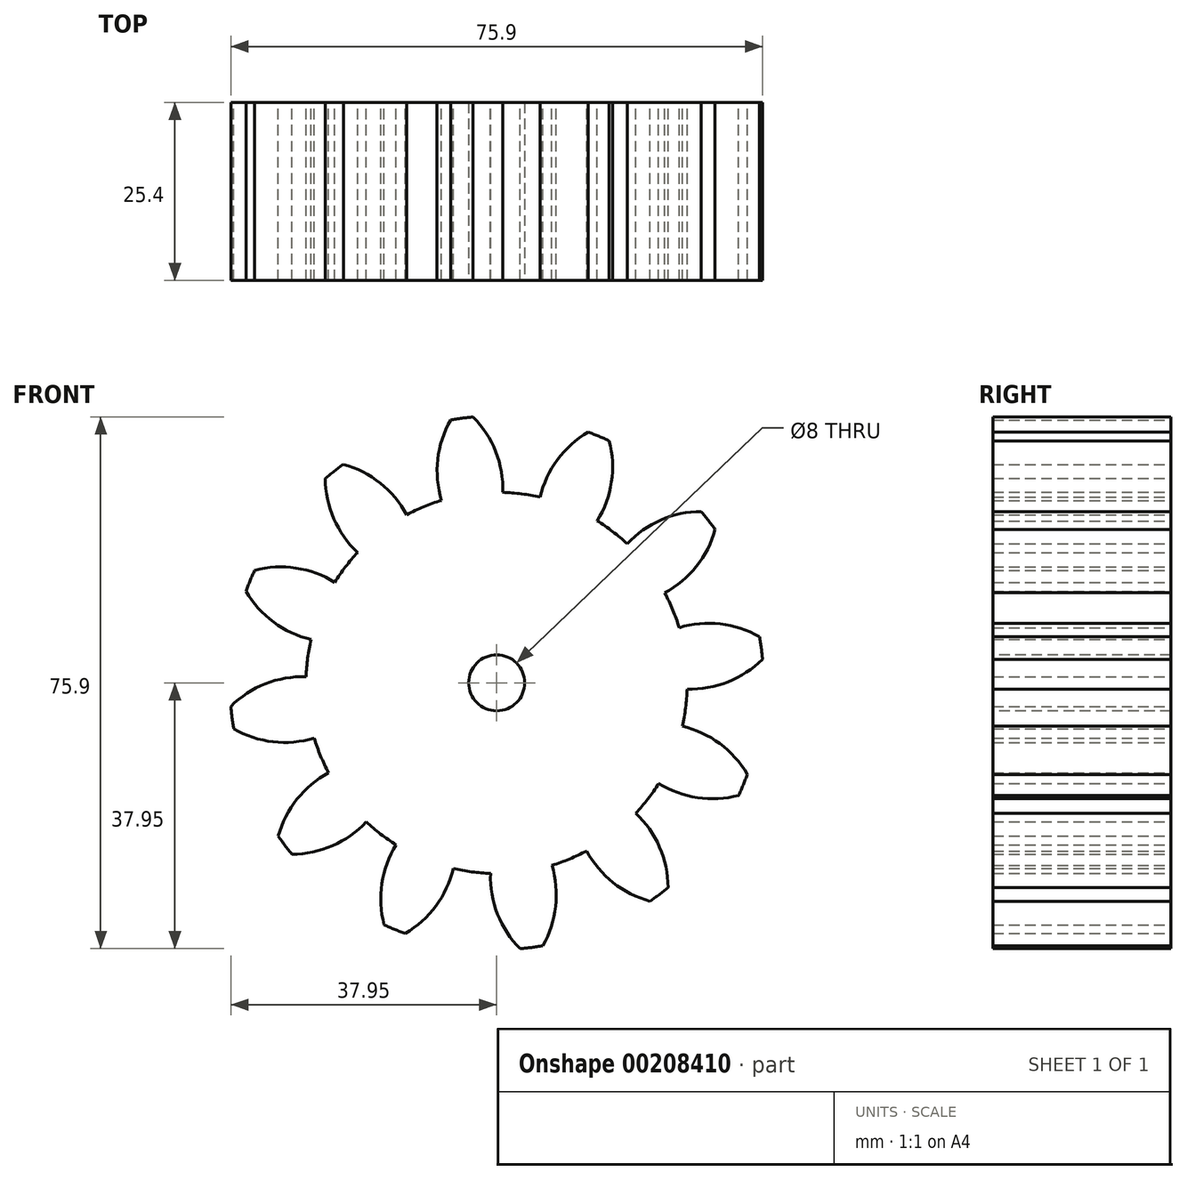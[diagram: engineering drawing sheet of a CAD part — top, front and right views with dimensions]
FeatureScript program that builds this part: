
annotation { "Feature Type Name" : "Feature", "Feature Type Description" : "" }
export const myFeature = defineFeature(function(context is Context, id is Id, definition is map)
    precondition{}
    {
        {
            assignVariable(context, id + "F0", {"name" : "NOT", "anyValue" : 12});
        }
        {
            var Q0;
            Q0=qCreatedBy(makeId("Front.planeOp"),FACE);
            var sketch = newSketch(context, id + "F1", { "sketchPlane" : qUnion([Q0])});
            skCircle(sketch, "E0", {"center": v(0, 0) * mm, "radius": 38.1 * mm});
            skCircle(sketch, "E1", {"center": v(0, 0) * mm, "radius": 32.66 * mm});
            skCircle(sketch, "E2", {"center": v(0, 0) * mm, "radius": 27.21 * mm});
            skLineSegment(sketch, "E3", {"start": v(0, 0) * mm, "end": v(0, 56.5) * mm});
            skLineSegment(sketch, "E4", {"start": v(0, 0) * mm, "end": v(-7.42, 56.35) * mm});
            skLineSegment(sketch, "E5", {"start": v(0, 32.66) * mm, "end": v(-56.68, 32.66) * mm});
            skLineSegment(sketch, "E6", {"start": v(0, 32.66) * mm, "end": v(-52.94, 13.39) * mm});
            skCircle(sketch, "E7", {"center": v(0, 32.66) * mm, "radius": 14.6 * mm});
            skArc(sketch, "E8", {"start": v(0.87, 27.2) * mm, "mid": v(-0.13, 33.01) * mm, "end": v(-3.36, 37.95) * mm});
            skArc(sketch, "E9.MirrorCS", {"start": v(-7.88, 26.05) * mm, "mid": v(-8.41, 31.92) * mm, "end": v(-6.58, 37.53) * mm});
            skSolve(sketch);
        }
        {
            var Q0;
            {var subQ0=sQuery(id+"F1.wireOp",EDGE,"E3");var subQ1=sQuery(id+"F1.wireOp",EDGE,"E2");var subQ2=makeQuery(id+"F1.imprint","INTERSECT",VERTEX,{"derivedFrom":[subQ1,subQ0]});Q0=makeQuery(id+"F1.imprint","IMPRINT",FACE,{"disambiguationData":[TD([[makeQuery(id+"F1.imprint","IMPRINT",EDGE,{"disambiguationData":[TD([[subQ2,-1.0]])],"derivedFrom":subQ1}),-1.0]])]});}
            var Q1;
            {var subQ0=sQuery(id+"F1.wireOp",EDGE,"E9.MirrorCS");var subQ1=sQuery(id+"F1.wireOp",EDGE,"E2");var subQ2=makeQuery(id+"F1.imprint","INTERSECT",VERTEX,{"derivedFrom":[subQ1,subQ0]});Q1=makeQuery(id+"F1.imprint","IMPRINT",FACE,{"disambiguationData":[TD([[makeQuery(id+"F1.imprint","IMPRINT",EDGE,{"disambiguationData":[TD([[subQ2,1.0]])],"derivedFrom":subQ1}),-1.0]])]});}
            var Q2;
            {var subQ0=sQuery(id+"F1.wireOp",EDGE,"E4");var subQ1=sQuery(id+"F1.wireOp",EDGE,"E1");var subQ2=makeQuery(id+"F1.imprint","INTERSECT",VERTEX,{"derivedFrom":[subQ1,subQ0]});Q2=makeQuery(id+"F1.imprint","IMPRINT",FACE,{"disambiguationData":[TD([[makeQuery(id+"F1.imprint","IMPRINT",EDGE,{"disambiguationData":[TD([[subQ2,-1.0]])],"derivedFrom":subQ1}),1.0]])]});}
            var Q3;
            {var subQ0=sQuery(id+"F1.wireOp",EDGE,"E4");var subQ1=sQuery(id+"F1.wireOp",EDGE,"E1");var subQ2=makeQuery(id+"F1.imprint","INTERSECT",VERTEX,{"derivedFrom":[subQ1,subQ0]});Q3=makeQuery(id+"F1.imprint","IMPRINT",FACE,{"disambiguationData":[TD([[makeQuery(id+"F1.imprint","IMPRINT",EDGE,{"disambiguationData":[TD([[subQ2,-1.0]])],"derivedFrom":subQ1}),-1.0]])]});}
            var Q4;
            {var subQ1=sQuery(id+"F1.wireOp",EDGE,"E1");var subQ3=sQuery(id+"F1.wireOp",EDGE,"E4");var subQ4=makeQuery(id+"F1.imprint","INTERSECT",VERTEX,{"derivedFrom":[subQ1,subQ3]});Q4=makeQuery(id+"F1.imprint","IMPRINT",FACE,{"disambiguationData":[TD([[makeQuery(id+"F1.imprint","IMPRINT",EDGE,{"disambiguationData":[TD([[subQ4,1.0]])],"derivedFrom":subQ3}),-1.0]])]});}
            var Q5;
            {var subQ1=sQuery(id+"F1.wireOp",EDGE,"E1");var subQ3=sQuery(id+"F1.wireOp",EDGE,"E4");var subQ4=makeQuery(id+"F1.imprint","INTERSECT",VERTEX,{"derivedFrom":[subQ1,subQ3]});Q5=makeQuery(id+"F1.imprint","IMPRINT",FACE,{"disambiguationData":[TD([[makeQuery(id+"F1.imprint","IMPRINT",EDGE,{"disambiguationData":[TD([[subQ4,-1.0]])],"derivedFrom":subQ3}),-1.0]])]});}
            var Q6;
            {var subQ0=sQuery(id+"F1.wireOp",EDGE,"E8");var subQ1=sQuery(id+"F1.wireOp",EDGE,"E0");var subQ2=makeQuery(id+"F1.imprint","INTERSECT",VERTEX,{"derivedFrom":[subQ1,subQ0]});Q6=makeQuery(id+"F1.imprint","IMPRINT",FACE,{"disambiguationData":[TD([[makeQuery(id+"F1.imprint","IMPRINT",EDGE,{"disambiguationData":[TD([[subQ2,-1.0]])],"derivedFrom":subQ1}),1.0]])]});}
            var Q7;
            {var subQ0=sQuery(id+"F1.wireOp",EDGE,"E9.MirrorCS");var subQ1=sQuery(id+"F1.wireOp",EDGE,"E0");var subQ2=makeQuery(id+"F1.imprint","INTERSECT",VERTEX,{"derivedFrom":[subQ1,subQ0]});Q7=makeQuery(id+"F1.imprint","IMPRINT",FACE,{"disambiguationData":[TD([[makeQuery(id+"F1.imprint","IMPRINT",EDGE,{"disambiguationData":[TD([[subQ2,1.0]])],"derivedFrom":subQ1}),1.0]])]});}
            var Q8;
            {var subQ0=sQuery(id+"F1.wireOp",EDGE,"E8");var subQ1=sQuery(id+"F1.wireOp",EDGE,"E2");var subQ2=makeQuery(id+"F1.imprint","INTERSECT",VERTEX,{"derivedFrom":[subQ1,subQ0]});Q8=makeQuery(id+"F1.imprint","IMPRINT",FACE,{"disambiguationData":[TD([[makeQuery(id+"F1.imprint","IMPRINT",EDGE,{"disambiguationData":[TD([[subQ2,-1.0]])],"derivedFrom":subQ1}),-1.0]])]});}
            var Q9;
            {var subQ0=sQuery(id+"F1.wireOp",EDGE,"E7");var subQ1=sQuery(id+"F1.wireOp",EDGE,"E2");var subQ8=makeQuery(id+"F1.imprint","INTERSECT",VERTEX,{"disambiguationData":[OD(0.0)],"derivedFrom":[subQ1,subQ0]});Q9=makeQuery(id+"F1.imprint","IMPRINT",FACE,{"disambiguationData":[TD([[makeQuery(id+"F1.imprint","IMPRINT",EDGE,{"disambiguationData":[TD([[subQ8,1.0]])],"derivedFrom":subQ1}),1.0]])]});}
            var Q10;
            {var subQ0=sQuery(id+"F1.wireOp",EDGE,"E2");var subQ1=makeQuery(id+"F1.imprint","INTERSECT",VERTEX,{"derivedFrom":[subQ0,sQuery(id+"F1.wireOp",EDGE,"E9.MirrorCS")]});Q10=makeQuery(id+"F1.imprint","IMPRINT",FACE,{"disambiguationData":[TD([[makeQuery(id+"F1.imprint","IMPRINT",EDGE,{"disambiguationData":[TD([[subQ1,1.0]])],"derivedFrom":subQ0}),1.0]])]});}
            var Q11;
            {var subQ0=sQuery(id+"F1.wireOp",EDGE,"E3");var subQ1=sQuery(id+"F1.wireOp",EDGE,"E2");var subQ2=makeQuery(id+"F1.imprint","INTERSECT",VERTEX,{"derivedFrom":[subQ1,subQ0]});Q11=makeQuery(id+"F1.imprint","IMPRINT",FACE,{"disambiguationData":[TD([[makeQuery(id+"F1.imprint","IMPRINT",EDGE,{"disambiguationData":[TD([[subQ2,-1.0]])],"derivedFrom":subQ1}),1.0]])]});}
            var Q12;
            {var subQ0=sQuery(id+"F1.wireOp",EDGE,"E4");var subQ1=sQuery(id+"F1.wireOp",EDGE,"E3");var subQ2=makeQuery(id+"F1.imprint","INTERSECT",VERTEX,{"derivedFrom":[subQ1,subQ0]});Q12=makeQuery(id+"F1.imprint","IMPRINT",FACE,{"disambiguationData":[TD([[makeQuery(id+"F1.imprint","IMPRINT",EDGE,{"disambiguationData":[TD([[subQ2,-1.0]])],"derivedFrom":subQ1}),1.0]])]});}
            var Q13;
            {var subQ0=sQuery(id+"F1.wireOp",EDGE,"E2");var subQ1=makeQuery(id+"F1.imprint","INTERSECT",VERTEX,{"derivedFrom":[subQ0,sQuery(id+"F1.wireOp",EDGE,"E8")]});Q13=makeQuery(id+"F1.imprint","IMPRINT",FACE,{"disambiguationData":[TD([[makeQuery(id+"F1.imprint","IMPRINT",EDGE,{"disambiguationData":[TD([[subQ1,1.0]])],"derivedFrom":subQ0}),1.0]])]});}
            extrude(context, id + "F2", {"entities" : qUnion([Q0, Q1, Q2, Q3, Q4, Q5, Q6, Q7, Q8, Q9, Q10, Q11, Q12, Q13]), "depth" : 25.4 * mm, "symmetric" : true});
        }
        {
            var Q0;
            Q0=makeQuery(id+"F2.opExtrude","SWEPT_BODY",BODY,{"disambiguationData":[OSD([sQuery(id+"F1.wireOp",EDGE,"E0"),sQuery(id+"F1.wireOp",EDGE,"E2"),sQuery(id+"F1.wireOp",EDGE,"E8"),sQuery(id+"F1.wireOp",EDGE,"E9.MirrorCS")])]});
            var Q1;
            Q1=makeQuery(id+"F2.opExtrude","SWEPT_FACE",FACE,{"disambiguationData":[OSD([sQuery(id+"F1.wireOp",EDGE,"E2")])]});
            circularPattern(context, id + "F3", {"operationType" : NewBodyOperationType.ADD, "entities" : qUnion([Q0]), "axis" : qUnion([Q1]), "angle" : (360 / getVariable(context, 'NOT')) * degree, "instanceCount" : getVariable(context, 'NOT')});
        }
        {
            var Q0;
            {var subQ0=makeQuery(id+"F2.opExtrude","CAP_FACE",FACE,{"disambiguationData":[OSD([sQuery(id+"F1.wireOp",EDGE,"E0"),sQuery(id+"F1.wireOp",EDGE,"E2"),sQuery(id+"F1.wireOp",EDGE,"E8"),sQuery(id+"F1.wireOp",EDGE,"E9.MirrorCS")])],"isStart":false});Q0=makeQuery(id+"F3.boolean.opBoolean","MERGE",FACE,{"derivedFrom":[subQ0,makeQuery(id+"F3.opPattern","COPY",FACE,{"derivedFrom":subQ0,"instanceName":"1"}),makeQuery(id+"F3.opPattern","COPY",FACE,{"derivedFrom":subQ0,"instanceName":"2"}),makeQuery(id+"F3.opPattern","COPY",FACE,{"derivedFrom":subQ0,"instanceName":"3"}),makeQuery(id+"F3.opPattern","COPY",FACE,{"derivedFrom":subQ0,"instanceName":"4"}),makeQuery(id+"F3.opPattern","COPY",FACE,{"derivedFrom":subQ0,"instanceName":"5"}),makeQuery(id+"F3.opPattern","COPY",FACE,{"derivedFrom":subQ0,"instanceName":"6"}),makeQuery(id+"F3.opPattern","COPY",FACE,{"derivedFrom":subQ0,"instanceName":"7"}),makeQuery(id+"F3.opPattern","COPY",FACE,{"derivedFrom":subQ0,"instanceName":"8"}),makeQuery(id+"F3.opPattern","COPY",FACE,{"derivedFrom":subQ0,"instanceName":"9"}),makeQuery(id+"F3.opPattern","COPY",FACE,{"derivedFrom":subQ0,"instanceName":"10"}),makeQuery(id+"F3.opPattern","COPY",FACE,{"derivedFrom":subQ0,"instanceName":"11"})]});}
            var sketch = newSketch(context, id + "F4", { "sketchPlane" : qUnion([Q0])});
            skPoint(sketch, "E10", {"position": v(0, 0) * mm});
            skSolve(sketch);
        }
        {
            var Q0;
            Q0=sQuery(id+"F4.wireOp",VERTEX,"E10");
            var Q1;
            Q1=makeQuery(id+"F2.opExtrude","SWEPT_BODY",BODY,{"disambiguationData":[OSD([sQuery(id+"F1.wireOp",EDGE,"E0"),sQuery(id+"F1.wireOp",EDGE,"E2"),sQuery(id+"F1.wireOp",EDGE,"E8"),sQuery(id+"F1.wireOp",EDGE,"E9.MirrorCS")])]});
            hole(context, id + "F5", {"style" : HoleStyle.SIMPLE, "holeDiameter" : 8 * mm, "endStyle" : HoleEndStyle.THROUGH, "locations" : qUnion([Q0]), "scope" : qUnion([Q1]), "tappedDepth" : 12 * mm, "tapClearance" : 3});
        }
    });
